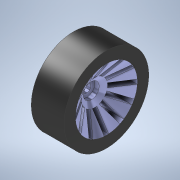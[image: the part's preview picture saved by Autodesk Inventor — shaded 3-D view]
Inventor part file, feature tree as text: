
AUTODESK INVENTOR PART (.ipt)
format: ipt  version: 2021 (Build 250183000, 183)  size: 252,928 bytes
history: native  units: mm
features: other x2, revolve x1, extrude x1, pattern_circular x1, sketch x1
ambient origin geometry x8: Origin, YZ Plane, XZ Plane, XY Plane, X Axis, Y Axis, Z Axis, Center Point
bodies: Volumenkörper1 (feature_tree)
feature tree (6):
  other  "00_Mastersketch.ipt"
  revolve  "Umdrehung1"
  extrude  "Extrusion1"  Depth=3.5mm
  pattern_circular  "Runde Anordnung1"  Angle=90.0deg  [1 undecoded]
  other  "05_wheelSketch"
  sketch  "Skizze2"  dims[d0=10.0mm d1=9.0mm d2=90.0deg d3=3.5mm d4=0.0mm d5=0.0mm d6=120.0mm d7=360.0deg d10=3.0mm d14=4.0mm]
note: 1 required parameter value undecoded (feature->parameter linkage not recoverable at this tier; creation-order binding heuristic only, values carry confidence <= 0.55)
